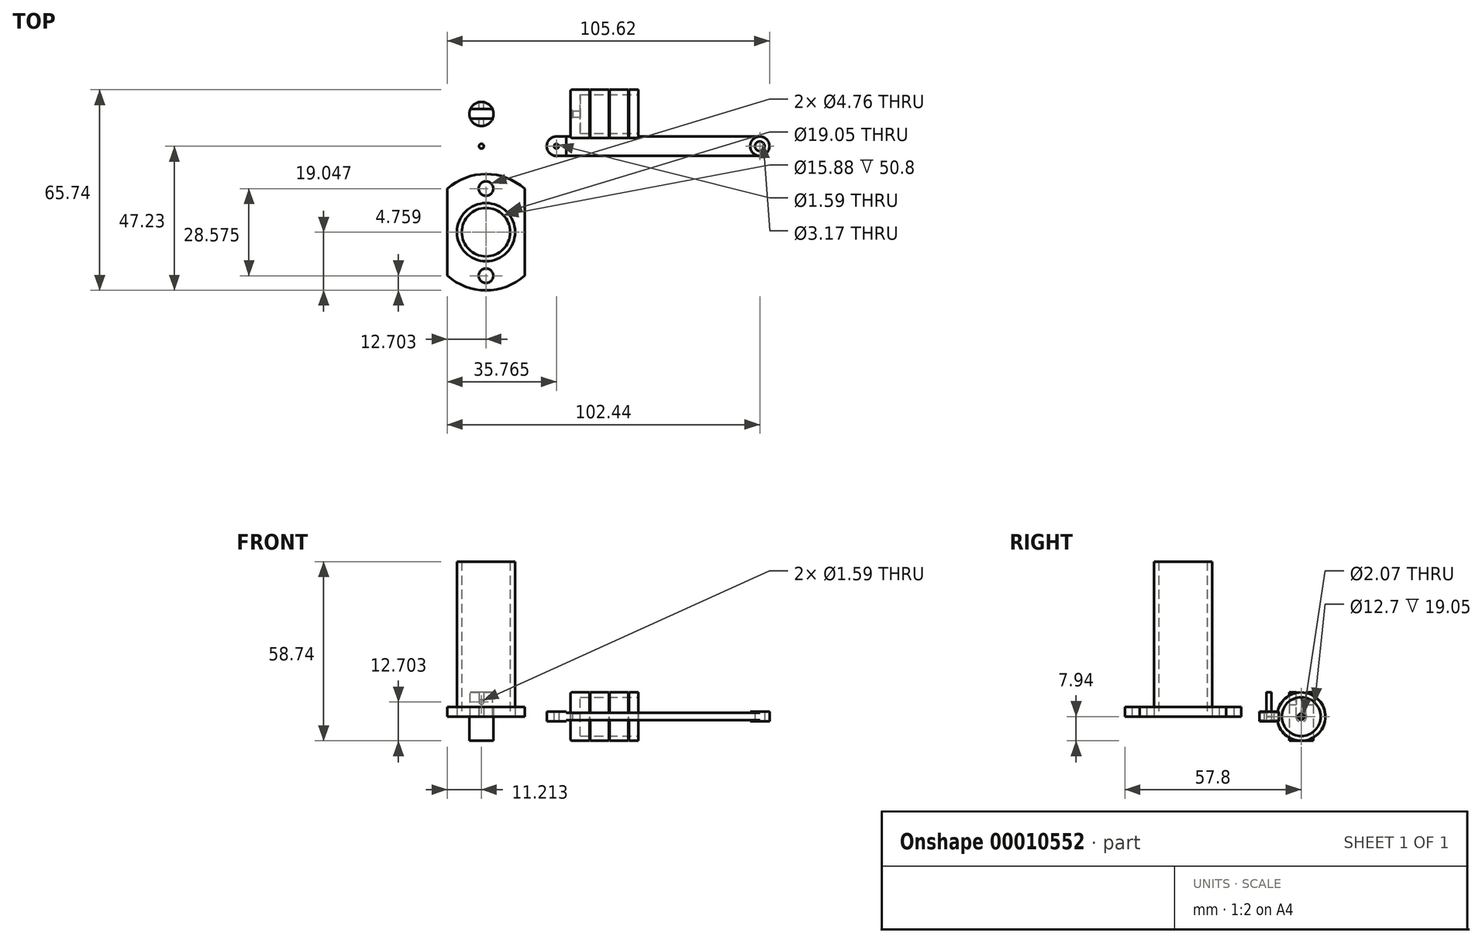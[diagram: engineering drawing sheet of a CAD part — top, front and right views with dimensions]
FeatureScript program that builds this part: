
annotation { "Feature Type Name" : "Feature", "Feature Type Description" : "" }
export const myFeature = defineFeature(function(context is Context, id is Id, definition is map)
    precondition{}
    {
        {
            var Q0;
            Q0=qCreatedBy(makeId("Top.planeOp"),FACE);
            var sketch = newSketch(context, id + "F0", { "sketchPlane" : qUnion([Q0])});
            skLineSegment(sketch, "E0", {"start": v(0, 0) * mm, "end": v(35.48, 0) * mm, "construction": true});
            skLineSegment(sketch, "E1.bottom", {"start": v(0, 0) * mm, "end": v(22.23, 0) * mm});
            skLineSegment(sketch, "E2.top", {"start": v(0, 0) * mm, "end": v(6.35, 0) * mm, "construction": true});
            skLineSegment(sketch, "E3.top", {"start": v(6.35, 0) * mm, "end": v(12.7, 0) * mm, "construction": true});
            skLineSegment(sketch, "E4.top", {"start": v(12.7, 0) * mm, "end": v(19.05, 0) * mm, "construction": true});
            skPoint(sketch, "E5.visualSharp", {"position": v(0, 7.94) * mm});
            skArc(sketch, "E5.filletArc", {"start": v(0.5, 7.94) * mm, "mid": v(0.15, 7.79) * mm, "end": v(0, 7.43) * mm});
            skLineSegment(sketch, "E6", {"start": v(6.35, 7.68) * mm, "end": v(6.5, 7.94) * mm});
            skLineSegment(sketch, "E7", {"start": v(6.35, 7.68) * mm, "end": v(6.19, 7.94) * mm});
            skLineSegment(sketch, "E8", {"start": v(12.7, 7.68) * mm, "end": v(12.85, 7.94) * mm});
            skLineSegment(sketch, "E9", {"start": v(12.7, 7.68) * mm, "end": v(12.53, 7.94) * mm});
            skLineSegment(sketch, "E10", {"start": v(19.05, 7.68) * mm, "end": v(19.2, 7.94) * mm});
            skLineSegment(sketch, "E11", {"start": v(19.05, 7.68) * mm, "end": v(18.88, 7.94) * mm});
            skLineSegment(sketch, "E12", {"start": v(0.5, 7.94) * mm, "end": v(6.19, 7.94) * mm});
            skLineSegment(sketch, "E13", {"start": v(6.5, 7.94) * mm, "end": v(12.53, 7.94) * mm});
            skLineSegment(sketch, "E14", {"start": v(12.85, 7.94) * mm, "end": v(18.88, 7.94) * mm});
            skLineSegment(sketch, "E15", {"start": v(19.2, 7.94) * mm, "end": v(22.23, 7.94) * mm});
            skLineSegment(sketch, "E16.bottom", {"start": v(22.23, 0) * mm, "end": v(3.05, 0) * mm});
            skLineSegment(sketch, "E16.top", {"start": v(22.23, 6.35) * mm, "end": v(3.18, 6.35) * mm});
            skLineSegment(sketch, "E17.top", {"start": v(3.05, 0) * mm, "end": v(0, 0) * mm});
            skLineSegment(sketch, "E18", {"start": v(22.23, 7.94) * mm, "end": v(22.23, 6.35) * mm});
            skLineSegment(sketch, "E19", {"start": v(3.18, 6.35) * mm, "end": v(3.18, 1.04) * mm});
            skLineSegment(sketch, "E20", {"start": v(0, 1.76) * mm, "end": v(0.73, 1.04) * mm});
            skLineSegment(sketch, "E21", {"start": v(0.73, 1.04) * mm, "end": v(3.18, 1.04) * mm});
            skLineSegment(sketch, "E22", {"start": v(0, 7.43) * mm, "end": v(0, 1.76) * mm});
            skLineSegment(sketch, "E23.rect.bottom", {"start": v(-25.13, -1.59) * mm, "end": v(-33.22, -1.59) * mm});
            skLineSegment(sketch, "E23.rect.top", {"start": v(-25.13, 1.59) * mm, "end": v(-33.22, 1.59) * mm});
            skLineSegment(sketch, "E23.rect.left", {"start": v(-25.13, -1.59) * mm, "end": v(-25.13, 1.59) * mm});
            skLineSegment(sketch, "E23.rect.right", {"start": v(-33.22, -1.59) * mm, "end": v(-33.22, 1.59) * mm});
            skPoint(sketch, "E23.rect.middle", {"position": v(-29.18, 0) * mm});
            skCircle(sketch, "E24", {"center": v(-29.18, 0) * mm, "radius": 3.97 * mm});
            skLineSegment(sketch, "E25.bottom", {"start": v(-4.62, -7.4) * mm, "end": v(62.05, -7.4) * mm});
            skLineSegment(sketch, "E25.top", {"start": v(-4.62, -13.75) * mm, "end": v(62.05, -13.75) * mm});
            skLineSegment(sketch, "E25.left", {"start": v(-7.8, -10.57) * mm, "end": v(-7.8, -10.57) * mm});
            skLineSegment(sketch, "E25.right", {"start": v(65.23, -10.57) * mm, "end": v(65.23, -10.57) * mm});
            skPoint(sketch, "E26.visualSharp", {"position": v(-7.8, -7.4) * mm});
            skArc(sketch, "E26.filletArc", {"start": v(-4.62, -7.4) * mm, "mid": v(-6.87, -8.33) * mm, "end": v(-7.8, -10.57) * mm});
            skPoint(sketch, "E27.visualSharp", {"position": v(65.23, -7.4) * mm});
            skArc(sketch, "E27.filletArc", {"start": v(65.23, -10.57) * mm, "mid": v(64.3, -8.33) * mm, "end": v(62.05, -7.4) * mm});
            skPoint(sketch, "E28.visualSharp", {"position": v(-7.8, -13.75) * mm});
            skArc(sketch, "E28.filletArc", {"start": v(-7.8, -10.57) * mm, "mid": v(-6.87, -12.82) * mm, "end": v(-4.62, -13.75) * mm});
            skPoint(sketch, "E29.visualSharp", {"position": v(65.23, -13.75) * mm});
            skArc(sketch, "E29.filletArc", {"start": v(62.05, -13.75) * mm, "mid": v(64.3, -12.82) * mm, "end": v(65.23, -10.57) * mm});
            skArc(sketch, "E30", {"start": v(62.05, -7.4) * mm, "mid": v(58.88, -10.57) * mm, "end": v(62.05, -13.75) * mm});
            skLineSegment(sketch, "E31", {"start": v(-1.45, -13.75) * mm, "end": v(-1.45, -7.4) * mm});
            skCircle(sketch, "E32", {"center": v(62.05, -10.57) * mm, "radius": 1.59 * mm});
            skCircle(sketch, "E33", {"center": v(-4.62, -10.57) * mm, "radius": 0.8 * mm});
            skCircle(sketch, "E34", {"center": v(-29.18, -10.57) * mm, "radius": 0.8 * mm});
            skSolve(sketch);
        }
        {
            var Q0;
            Q0=makeQuery(id+"F0.imprint","IMPRINT",FACE,{"disambiguationData":[TD([[makeQuery(id+"F0.imprint","IMPRINT",EDGE,{"derivedFrom":sQuery(id+"F0.wireOp",EDGE,"E5.filletArc")}),1.0]])]});
            var Q1;
            Q1=sQuery(id+"F0.wireOp",EDGE,"E16.bottom");
            revolve(context, id + "F1", {"entities" : qUnion([Q0]), "axis" : qUnion([Q1]), "revolveType" : RevolveType.FULL});
        }
        {
            var Q0;
            {var subQ0=sQuery(id+"F0.wireOp",EDGE,"E24");var subQ1=sQuery(id+"F0.wireOp",EDGE,"E23.rect.bottom");var subQ3=makeQuery(id+"F0.imprint","INTERSECT",VERTEX,{"disambiguationData":[OD(0.0)],"derivedFrom":[subQ1,subQ0]});Q0=makeQuery(id+"F0.imprint","IMPRINT",FACE,{"disambiguationData":[TD([[makeQuery(id+"F0.imprint","IMPRINT",EDGE,{"disambiguationData":[TD([[subQ3,-1.0]])],"derivedFrom":subQ1}),1.0]])]});}
            var Q1;
            {var subQ0=sQuery(id+"F0.wireOp",EDGE,"E24");var subQ3=sQuery(id+"F0.wireOp",EDGE,"E23.rect.bottom");var subQ4=makeQuery(id+"F0.imprint","INTERSECT",VERTEX,{"disambiguationData":[OD(0.0)],"derivedFrom":[subQ3,subQ0]});Q1=makeQuery(id+"F0.imprint","IMPRINT",FACE,{"disambiguationData":[TD([[makeQuery(id+"F0.imprint","IMPRINT",EDGE,{"disambiguationData":[TD([[subQ4,-1.0]])],"derivedFrom":subQ3}),-1.0]])]});}
            var Q2;
            {var subQ0=sQuery(id+"F0.wireOp",EDGE,"E24");var subQ1=sQuery(id+"F0.wireOp",EDGE,"E23.rect.top");var subQ3=makeQuery(id+"F0.imprint","INTERSECT",VERTEX,{"disambiguationData":[OD(0.0)],"derivedFrom":[subQ1,subQ0]});Q2=makeQuery(id+"F0.imprint","IMPRINT",FACE,{"disambiguationData":[TD([[makeQuery(id+"F0.imprint","IMPRINT",EDGE,{"disambiguationData":[TD([[subQ3,-1.0]])],"derivedFrom":subQ1}),-1.0]])]});}
            extrude(context, id + "F2", {"entities" : qUnion([Q0, Q1, Q2]), "depth" : 7.94 * mm, "hasSecondDirection" : true, "secondDirectionOppositeDirection" : true, "secondDirectionDepth" : 7.94 * mm});
        }
        {
            var Q0;
            Q0=makeQuery(id+"F2.opExtrude","CAP_FACE",FACE,{"disambiguationData":[OSD([sQuery(id+"F0.wireOp",EDGE,"E24")])],"isStart":false});
            var sketch = newSketch(context, id + "F3", { "sketchPlane" : qUnion([Q0])});
            skLineSegment(sketch, "E35.rect.bottom", {"start": v(-24.76, -1.59) * mm, "end": v(-33.6, -1.59) * mm});
            skLineSegment(sketch, "E35.rect.top", {"start": v(-24.76, 1.59) * mm, "end": v(-33.6, 1.59) * mm});
            skLineSegment(sketch, "E35.rect.left", {"start": v(-24.76, -1.59) * mm, "end": v(-24.76, 1.59) * mm});
            skLineSegment(sketch, "E35.rect.right", {"start": v(-33.6, -1.59) * mm, "end": v(-33.6, 1.59) * mm});
            skPoint(sketch, "E35.rect.middle", {"position": v(-29.18, 0) * mm});
            skSolve(sketch);
        }
        {
            var Q0;
            {var subQ0=makeQuery(id+"F2.opExtrude","CAP_EDGE",EDGE,{"disambiguationData":[OSD([sQuery(id+"F0.wireOp",EDGE,"E24")])],"isStart":false});var subQ3=sQuery(id+"F3.wireOp",EDGE,"E35.rect.bottom");var subQ6=makeQuery(id+"F3.imprint","INTERSECT",VERTEX,{"disambiguationData":[OD(0.0)],"derivedFrom":[subQ0,subQ3]});Q0=makeQuery(id+"F3.imprint","IMPRINT",FACE,{"disambiguationData":[TD([[makeQuery(id+"F3.imprint","IMPRINT",EDGE,{"disambiguationData":[TD([[subQ6,-1.0]])],"derivedFrom":subQ3}),-1.0]])]});}
            extrude(context, id + "F4", {"entities" : qUnion([Q0]), "operationType" : NewBodyOperationType.REMOVE, "oppositeDirection" : true, "depth" : 7.94 * mm});
        }
        {
            var Q0;
            Q0=makeQuery(id+"F4.boolean.opBoolean","COPY",FACE,{"derivedFrom":makeQuery(id+"F4.opExtrude","SWEPT_FACE",FACE,{"disambiguationData":[OSD([sQuery(id+"F3.wireOp",EDGE,"E35.rect.bottom")])]})});
            var sketch = newSketch(context, id + "F5", { "sketchPlane" : qUnion([Q0])});
            skLineSegment(sketch, "E36", {"start": v(22.27, 4.76) * mm, "end": v(40.04, 4.76) * mm, "construction": true});
            skLineSegment(sketch, "E37", {"start": v(29.18, 7.94) * mm, "end": v(29.18, 4.76) * mm, "construction": true});
            skCircle(sketch, "E38", {"center": v(29.18, 4.76) * mm, "radius": 0.8 * mm});
            skSolve(sketch);
        }
        {
            var Q0;
            Q0=makeQuery(id+"F5.imprint","IMPRINT",FACE,{"disambiguationData":[TD([[makeQuery(id+"F5.imprint","IMPRINT",EDGE,{"derivedFrom":sQuery(id+"F5.wireOp",EDGE,"E38")}),1.0]])]});
            extrude(context, id + "F6", {"entities" : qUnion([Q0]), "operationType" : NewBodyOperationType.REMOVE, "oppositeDirection" : true, "depth" : 25.4 * mm, "hasSecondDirection" : true, "secondDirectionOppositeDirection" : false, "secondDirectionDepth" : 25.4 * mm});
        }
        {
            var Q0;
            {var subQ2=sQuery(id+"F0.wireOp",EDGE,"E26.filletArc");Q0=makeQuery(id+"F0.imprint","IMPRINT",FACE,{"disambiguationData":[TD([[makeQuery(id+"F0.imprint","IMPRINT",EDGE,{"derivedFrom":subQ2}),1.0]])]});}
            extrude(context, id + "F7", {"entities" : qUnion([Q0]), "depth" : 3.17 * mm, "symmetric" : true});
        }
        {
            var Q0;
            {var subQ2=sQuery(id+"F0.wireOp",EDGE,"E30");Q0=makeQuery(id+"F0.imprint","IMPRINT",FACE,{"disambiguationData":[TD([[makeQuery(id+"F0.imprint","IMPRINT",EDGE,{"derivedFrom":subQ2}),-1.0]])]});}
            extrude(context, id + "F8", {"entities" : qUnion([Q0]), "operationType" : NewBodyOperationType.ADD, "depth" : 2.38 * mm, "symmetric" : true});
        }
        {
            var Q0;
            Q0=makeQuery(id+"F0.imprint","IMPRINT",FACE,{"disambiguationData":[TD([[makeQuery(id+"F0.imprint","IMPRINT",EDGE,{"derivedFrom":sQuery(id+"F0.wireOp",EDGE,"E27.filletArc")}),1.0]])]});
            extrude(context, id + "F9", {"entities" : qUnion([Q0]), "operationType" : NewBodyOperationType.ADD, "depth" : 3.17 * mm, "symmetric" : true});
        }
        {
            var Q0;
            Q0=makeQuery(id+"F0.imprint","IMPRINT",FACE,{"disambiguationData":[TD([[makeQuery(id+"F0.imprint","IMPRINT",EDGE,{"derivedFrom":sQuery(id+"F0.wireOp",EDGE,"E34")}),1.0]])]});
            extrude(context, id + "F10", {"entities" : qUnion([Q0]), "depth" : 7.94 * mm});
        }
        {
            var Q0;
            Q0=qCreatedBy(makeId("Top.planeOp"),FACE);
            var sketch = newSketch(context, id + "F11", { "sketchPlane" : qUnion([Q0])});
            skCircle(sketch, "E39", {"center": v(-27.69, -38.75) * mm, "radius": 9.53 * mm});
            skCircle(sketch, "E40", {"center": v(-27.69, -38.75) * mm, "radius": 7.94 * mm});
            skCircle(sketch, "E41", {"center": v(-27.69, -38.75) * mm, "radius": 19.05 * mm});
            skLineSegment(sketch, "E42.rect.bottom", {"start": v(-14.99, -61.02) * mm, "end": v(-40.39, -61.02) * mm});
            skLineSegment(sketch, "E42.rect.top", {"start": v(-14.99, -16.48) * mm, "end": v(-40.39, -16.48) * mm});
            skLineSegment(sketch, "E42.rect.left", {"start": v(-14.99, -61.02) * mm, "end": v(-14.99, -16.48) * mm});
            skLineSegment(sketch, "E42.rect.right", {"start": v(-40.39, -61.02) * mm, "end": v(-40.39, -16.48) * mm});
            skCircle(sketch, "E43", {"center": v(-27.69, -38.75) * mm, "radius": 14.29 * mm, "construction": true});
            skCircle(sketch, "E44", {"center": v(-27.69, -24.47) * mm, "radius": 2.38 * mm});
            skCircle(sketch, "E45", {"center": v(-27.69, -53.04) * mm, "radius": 2.38 * mm});
            skSolve(sketch);
        }
        {
            var Q0;
            Q0=makeQuery(id+"F11.imprint","IMPRINT",FACE,{"disambiguationData":[TD([[makeQuery(id+"F11.imprint","IMPRINT",EDGE,{"derivedFrom":sQuery(id+"F11.wireOp",EDGE,"E39")}),1.0]])]});
            extrude(context, id + "F12", {"entities" : qUnion([Q0]), "depth" : 50.8 * mm});
        }
        {
            var Q0;
            Q0=makeQuery(id+"F11.imprint","IMPRINT",FACE,{"disambiguationData":[TD([[makeQuery(id+"F11.imprint","IMPRINT",EDGE,{"derivedFrom":sQuery(id+"F11.wireOp",EDGE,"E39")}),-1.0]])]});
            extrude(context, id + "F13", {"entities" : qUnion([Q0]), "depth" : 3.17 * mm, "offsetDistance" : 25.4 * mm});
        }
    });
